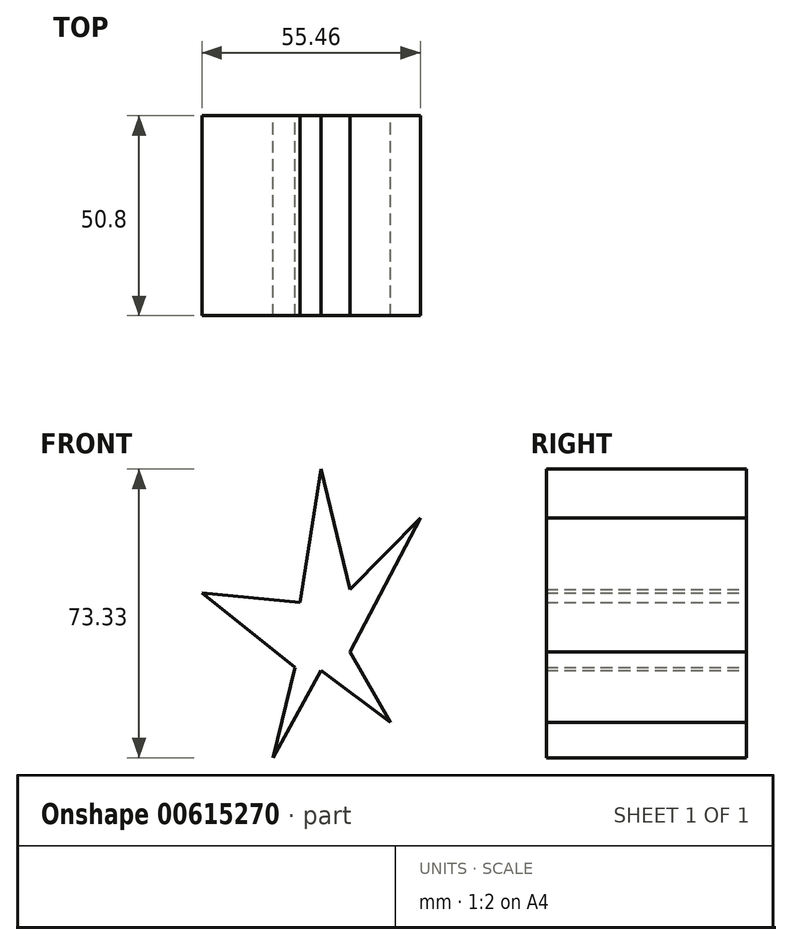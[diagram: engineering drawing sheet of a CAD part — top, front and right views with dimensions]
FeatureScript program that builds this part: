
annotation { "Feature Type Name" : "Feature", "Feature Type Description" : "" }
export const myFeature = defineFeature(function(context is Context, id is Id, definition is map)
    precondition{}
    {
        {
            var Q0;
            Q0=qCreatedBy(makeId("Front.planeOp"),FACE);
            var sketch = newSketch(context, id + "F0", { "sketchPlane" : qUnion([Q0])});
            skLineSegment(sketch, "E0", {"start": v(-7.38, 46.4) * mm, "end": v(0, 15.78) * mm});
            skLineSegment(sketch, "E1", {"start": v(0, 15.78) * mm, "end": v(17.87, 34.01) * mm});
            skLineSegment(sketch, "E2", {"start": v(17.87, 34.01) * mm, "end": v(0, 0) * mm});
            skLineSegment(sketch, "E3", {"start": v(0, 0) * mm, "end": v(10.33, -18) * mm});
            skLineSegment(sketch, "E4", {"start": v(10.33, -18) * mm, "end": v(-7.38, -4.8) * mm});
            skLineSegment(sketch, "E5", {"start": v(-7.38, -4.8) * mm, "end": v(-19.5, -26.94) * mm});
            skLineSegment(sketch, "E6", {"start": v(-19.5, -26.94) * mm, "end": v(-13.93, -4.02) * mm});
            skLineSegment(sketch, "E7", {"start": v(-13.93, -4.02) * mm, "end": v(-37.59, 14.94) * mm});
            skLineSegment(sketch, "E8", {"start": v(-7.38, 46.4) * mm, "end": v(-12.73, 12.47) * mm});
            skLineSegment(sketch, "E9", {"start": v(-37.59, 14.94) * mm, "end": v(-12.73, 12.47) * mm});
            skSolve(sketch);
        }
        {
            var Q0;
            Q0=makeQuery(id+"F0.imprint","IMPRINT",FACE,{"disambiguationData":[TD([[makeQuery(id+"F0.imprint","IMPRINT",EDGE,{"derivedFrom":sQuery(id+"F0.wireOp",EDGE,"E0")}),-1.0]])]});
            var Q1;
            Q1 = qSketchRegion(id + "F0", true);
            extrude(context, id + "F1", {"entities" : qUnion([Q0, Q1]), "depth" : 50.8 * mm, "offsetDistance" : 25.4 * mm});
        }
    });
